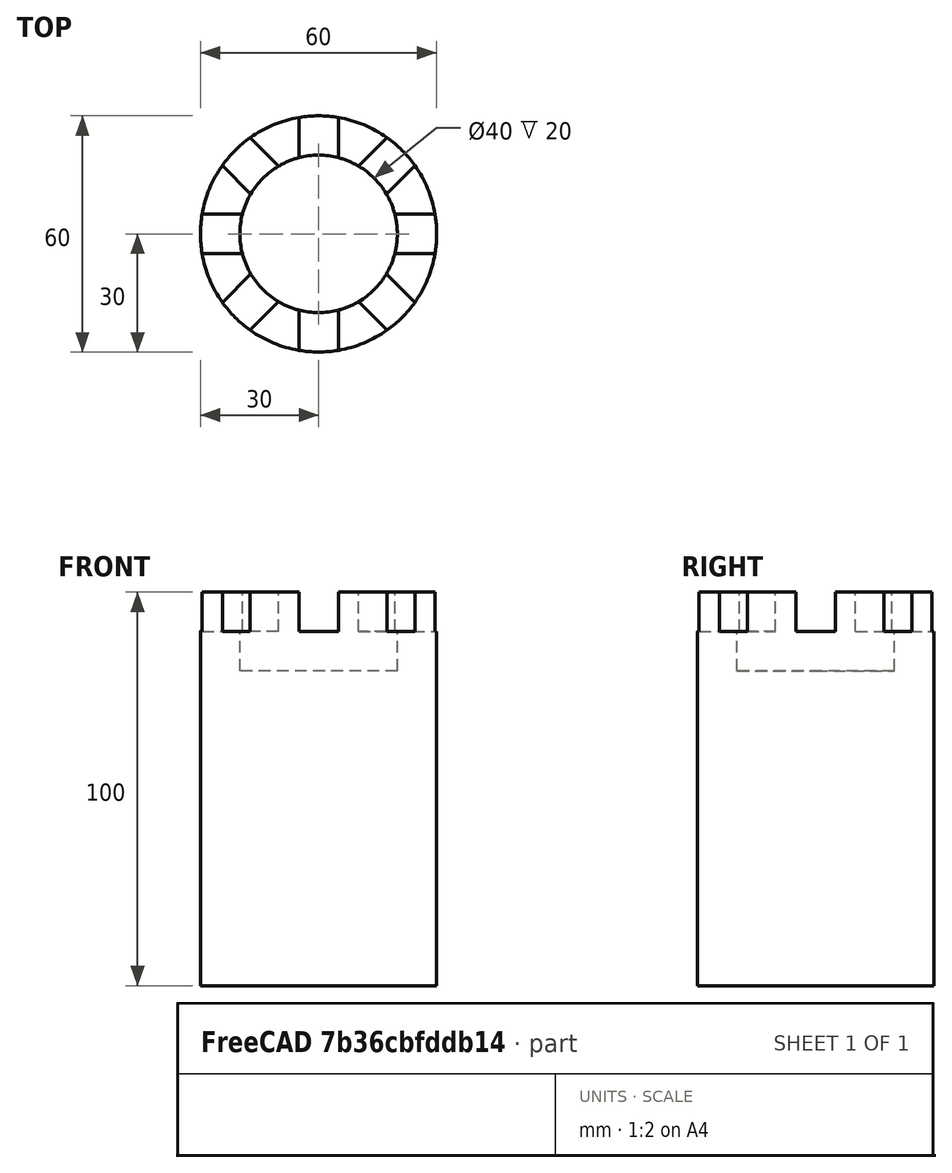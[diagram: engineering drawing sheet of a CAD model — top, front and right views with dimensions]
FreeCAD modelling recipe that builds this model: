
FCSTD DOCUMENT  (FreeCAD 0.18.4R)
Label: tutorial_freecad_ex11_d
License: All rights reserved
LicenseURL: http://en.wikipedia.org/wiki/All_rights_reserved
objects: Part::Cylinder×2, Part::Cut×2, Part::Box×1, Part::FeaturePython×1, Part::MultiFuse×1
note: 7 computed .brp shape members not serialized (recipe doc carries the construction recipe); baked Part::Feature solids carry a one-line shape summary decoded from their .brp

FEATURE [Part::Cylinder] Cylinder  label="base"
  Angle = 360
  AttacherType = Attacher::AttachEngine3D
  Height = 100
  Radius = 30
FEATURE [Part::Cylinder] Cylinder001  label="resta_azotea"
  Angle = 360
  AttacherType = Attacher::AttachEngine3D
  Height = 30
  Placement = pos=(0,0,80) rot=(0,0,1;0rad)
  Radius = 20
FEATURE [Part::Cut] Cut
  Base = -> Cylinder
  Refine = true
  Tool = -> Cylinder001
FEATURE [Part::Box] Box  label="Cubo"
  AttacherType = Attacher::AttachEngine3D
  Height = 11
  Length = 70
  Placement = pos=(-35,-5,90) rot=(0,0,1;0rad)
  Width = 10
FEATURE [Part::FeaturePython] Array  # Draft array (typed FeaturePython)
  Angle = 360
  ArrayType = 1
  Axis = (0,0,1)
  Base = -> Box
  Center = (0,0,0)
  Fuse = false
  IntervalAxis = (0,0,0)
  IntervalX = (1,0,0)
  IntervalY = (0,1,0)
  IntervalZ = (0,0,1)
  NumberPolar = 8
  NumberX = 2
  NumberY = 2
  NumberZ = 1
FEATURE [Part::MultiFuse] Fusion
  Refine = true
  Shapes = -> [Array]
FEATURE [Part::Cut] Cut001
  Base = -> Cut
  Refine = true
  Tool = -> Fusion
